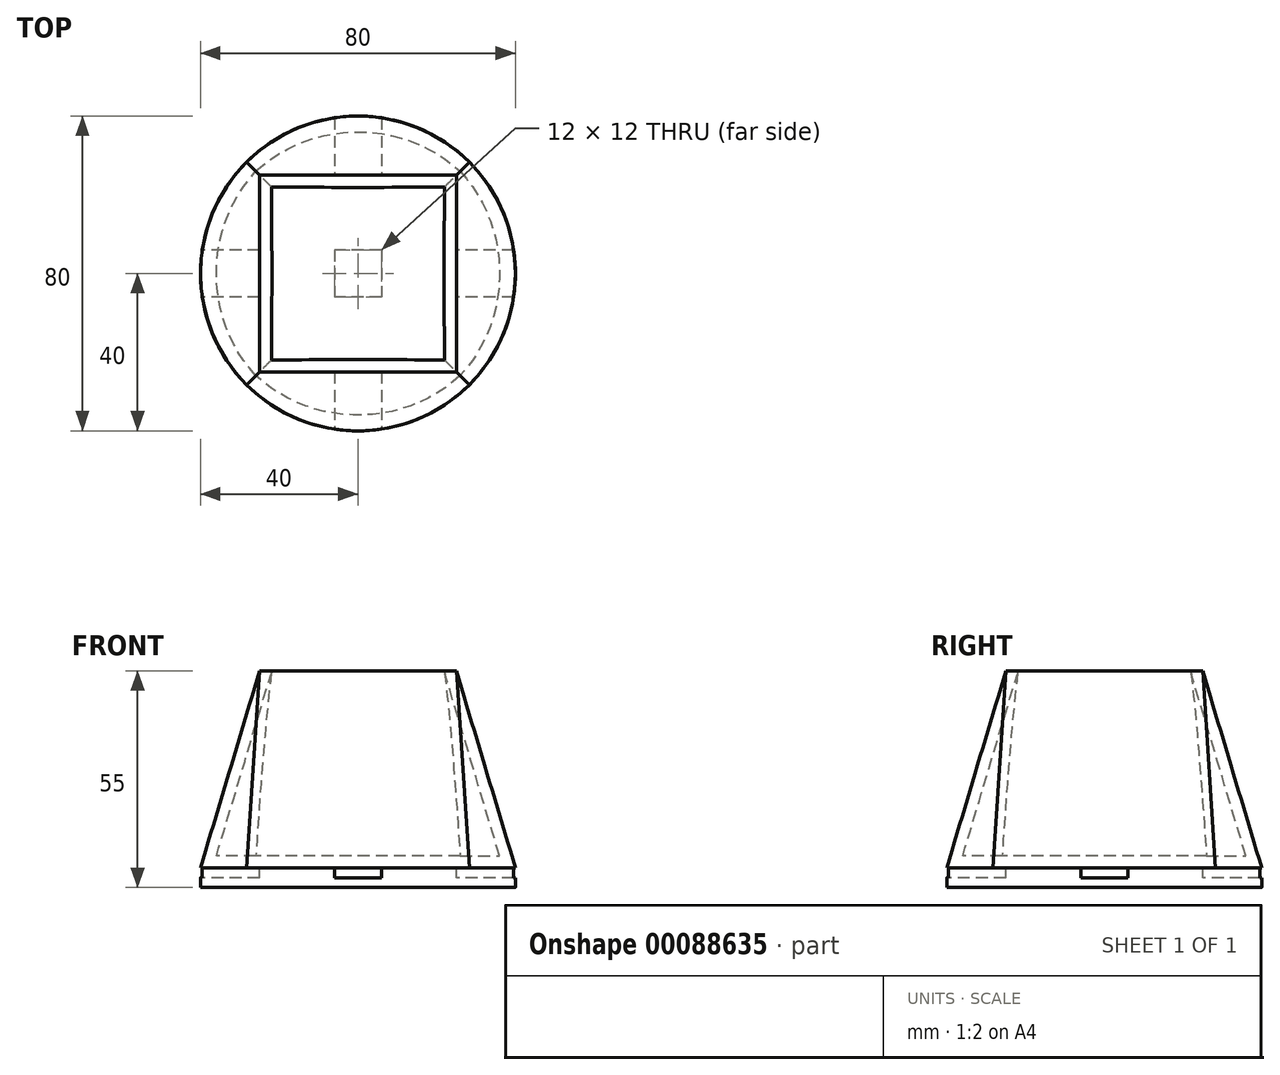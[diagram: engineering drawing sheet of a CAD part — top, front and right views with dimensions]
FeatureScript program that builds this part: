
annotation { "Feature Type Name" : "Feature", "Feature Type Description" : "" }
export const myFeature = defineFeature(function(context is Context, id is Id, definition is map)
    precondition{}
    {
        {
            var Q0;
            Q0=qCreatedBy(makeId("Top.planeOp"),FACE);
            var sketch = newSketch(context, id + "F0", { "sketchPlane" : qUnion([Q0])});
            skCircle(sketch, "E0", {"center": v(0, 0) * mm, "radius": 40 * mm});
            skSolve(sketch);
        }
        {
            var Q0;
            Q0=qCreatedBy(makeId("Top.planeOp"),FACE);
            cPlane(context, id + "F1", {"entities" : qUnion([Q0]), "cplaneType" : CPlaneType.OFFSET, "offset" : 50 * mm, "width" : 152.4 * mm, "height" : 152.4 * mm});
        }
        {
            var Q0;
            Q0=qCreatedBy(id+"F1.planeOp",FACE);
            var sketch = newSketch(context, id + "F2", { "sketchPlane" : qUnion([Q0])});
            skLineSegment(sketch, "E1.bottom", {"start": v(-25, -25) * mm, "end": v(25, -25) * mm});
            skLineSegment(sketch, "E1.top", {"start": v(-25, 25) * mm, "end": v(25, 25) * mm});
            skLineSegment(sketch, "E1.left", {"start": v(-25, -25) * mm, "end": v(-25, 25) * mm});
            skLineSegment(sketch, "E1.right", {"start": v(25, -25) * mm, "end": v(25, 25) * mm});
            skPoint(sketch, "E1.middle", {"position": v(0, 0) * mm});
            skSolve(sketch);
        }
        {
            var Q0;
            Q0=makeQuery(id+"F2.imprint","IMPRINT",FACE,{"disambiguationData":[TD([[makeQuery(id+"F2.imprint","IMPRINT",EDGE,{"derivedFrom":sQuery(id+"F2.wireOp",EDGE,"E1.bottom")}),1.0]])]});
            var Q1;
            Q1=makeQuery(id+"F0.imprint","IMPRINT",FACE,{"disambiguationData":[TD([[makeQuery(id+"F0.imprint","IMPRINT",EDGE,{"derivedFrom":sQuery(id+"F0.wireOp",EDGE,"E0")}),1.0]])]});
            loft(context, id + "F3", {"sheetProfilesArray" : [{ "sheetProfileEntities" : qUnion([Q0]) }, { "sheetProfileEntities" : qUnion([Q1]) }]});
        }
        {
            var Q0;
            Q0=makeQuery(id+"F3.opLoft","CAP_FACE",FACE,{"disambiguationData":[OSD([makeQuery(id+"F2.imprint","IMPRINT",FACE,{"disambiguationData":[TD([[makeQuery(id+"F2.imprint","IMPRINT",EDGE,{"derivedFrom":sQuery(id+"F2.wireOp",EDGE,"E1.bottom")}),1.0]])]})])],"isStart":true});
            shell(context, id + "F4", {"entities" : qUnion([Q0]), "thickness" : 3 * mm});
        }
        {
            var Q0;
            Q0=makeQuery(id+"F3.opLoft","CAP_FACE",FACE,{"disambiguationData":[OSD([makeQuery(id+"F0.imprint","IMPRINT",FACE,{"disambiguationData":[TD([[makeQuery(id+"F0.imprint","IMPRINT",EDGE,{"derivedFrom":sQuery(id+"F0.wireOp",EDGE,"E0")}),1.0]])]})])],"isStart":true});
            var sketch = newSketch(context, id + "F5", { "sketchPlane" : qUnion([Q0])});
            skCircle(sketch, "E2", {"center": v(0, 0) * mm, "radius": 40 * mm});
            skLineSegment(sketch, "E3.bottom", {"start": v(50, -6) * mm, "end": v(-50, -6) * mm});
            skLineSegment(sketch, "E3.top", {"start": v(50, 6) * mm, "end": v(-50, 6) * mm});
            skLineSegment(sketch, "E3.left", {"start": v(50, -6) * mm, "end": v(50, 6) * mm});
            skLineSegment(sketch, "E3.right", {"start": v(-50, -6) * mm, "end": v(-50, 6) * mm});
            skLineSegment(sketch, "E4.bottom", {"start": v(25, -6) * mm, "end": v(-25, -6) * mm});
            skLineSegment(sketch, "E4.top", {"start": v(25, 6) * mm, "end": v(-25, 6) * mm});
            skLineSegment(sketch, "E4.left", {"start": v(25, -6) * mm, "end": v(25, 6) * mm});
            skLineSegment(sketch, "E4.right", {"start": v(-25, -6) * mm, "end": v(-25, 6) * mm});
            skLineSegment(sketch, "E5.bottom", {"start": v(-6, -50) * mm, "end": v(6, -50) * mm});
            skLineSegment(sketch, "E5.top", {"start": v(-6, 50) * mm, "end": v(6, 50) * mm});
            skLineSegment(sketch, "E5.left", {"start": v(-6, -50) * mm, "end": v(-6, 50) * mm});
            skLineSegment(sketch, "E5.right", {"start": v(6, -50) * mm, "end": v(6, 50) * mm});
            skLineSegment(sketch, "E6.bottom", {"start": v(-6, -25) * mm, "end": v(6, -25) * mm});
            skLineSegment(sketch, "E6.top", {"start": v(-6, 25) * mm, "end": v(6, 25) * mm});
            skLineSegment(sketch, "E6.left", {"start": v(-6, -25) * mm, "end": v(-6, 25) * mm});
            skLineSegment(sketch, "E6.right", {"start": v(6, -25) * mm, "end": v(6, 25) * mm});
            skSolve(sketch);
        }
        {
            var Q0;
            {var subQ5=sQuery(id+"F5.wireOp",EDGE,"E2");var subQ6=makeQuery(id+"F5.imprint","IMPRINT",VERTEX,{"disambiguationData":[OD(1.0)],"derivedFrom":subQ5});Q0=makeQuery(id+"F5.imprint","IMPRINT",FACE,{"disambiguationData":[TD([[makeQuery(id+"F5.imprint","IMPRINT",EDGE,{"disambiguationData":[TD([[subQ6,-1.0]])],"derivedFrom":subQ5}),1.0]])]});}
            var Q1;
            {var subQ5=sQuery(id+"F5.wireOp",EDGE,"E6.bottom");Q1=makeQuery(id+"F5.imprint","IMPRINT",FACE,{"disambiguationData":[TD([[makeQuery(id+"F5.imprint","IMPRINT",EDGE,{"derivedFrom":subQ5}),-1.0]])]});}
            var Q2;
            {var subQ3=sQuery(id+"F5.wireOp",EDGE,"E2");var subQ5=makeQuery(id+"F5.imprint","IMPRINT",VERTEX,{"disambiguationData":[OD(0.0)],"derivedFrom":subQ3});Q2=makeQuery(id+"F5.imprint","IMPRINT",FACE,{"disambiguationData":[TD([[makeQuery(id+"F5.imprint","IMPRINT",EDGE,{"disambiguationData":[TD([[subQ5,-1.0]])],"derivedFrom":subQ3}),1.0]])]});}
            var Q3;
            {var subQ5=sQuery(id+"F5.wireOp",EDGE,"E6.bottom");Q3=makeQuery(id+"F5.imprint","IMPRINT",FACE,{"disambiguationData":[TD([[makeQuery(id+"F5.imprint","IMPRINT",EDGE,{"derivedFrom":subQ5}),1.0]])]});}
            var Q4;
            {var subQ0=sQuery(id+"F5.wireOp",EDGE,"E4.right");Q4=makeQuery(id+"F5.imprint","IMPRINT",FACE,{"disambiguationData":[TD([[makeQuery(id+"F5.imprint","IMPRINT",EDGE,{"derivedFrom":subQ0}),-1.0]])]});}
            var Q5;
            {var subQ5=sQuery(id+"F5.wireOp",EDGE,"E4.right");Q5=makeQuery(id+"F5.imprint","IMPRINT",FACE,{"disambiguationData":[TD([[makeQuery(id+"F5.imprint","IMPRINT",EDGE,{"derivedFrom":subQ5}),1.0]])]});}
            var Q6;
            {var subQ5=sQuery(id+"F5.wireOp",EDGE,"E2");var subQ6=makeQuery(id+"F5.imprint","IMPRINT",VERTEX,{"disambiguationData":[OD(3.0)],"derivedFrom":subQ5});Q6=makeQuery(id+"F5.imprint","IMPRINT",FACE,{"disambiguationData":[TD([[makeQuery(id+"F5.imprint","IMPRINT",EDGE,{"disambiguationData":[TD([[subQ6,-1.0]])],"derivedFrom":subQ5}),1.0]])]});}
            var Q7;
            {var subQ5=sQuery(id+"F5.wireOp",EDGE,"E6.top");Q7=makeQuery(id+"F5.imprint","IMPRINT",FACE,{"disambiguationData":[TD([[makeQuery(id+"F5.imprint","IMPRINT",EDGE,{"derivedFrom":subQ5}),-1.0]])]});}
            var Q8;
            {var subQ0=sQuery(id+"F5.wireOp",EDGE,"E6.right");var subQ1=sQuery(id+"F5.wireOp",EDGE,"E4.bottom");var subQ2=makeQuery(id+"F5.imprint","INTERSECT",VERTEX,{"derivedFrom":[subQ1,subQ0]});Q8=makeQuery(id+"F5.imprint","IMPRINT",FACE,{"disambiguationData":[TD([[makeQuery(id+"F5.imprint","IMPRINT",EDGE,{"disambiguationData":[TD([[subQ2,-1.0]])],"derivedFrom":subQ1}),-1.0]])]});}
            var Q9;
            {var subQ0=sQuery(id+"F5.wireOp",EDGE,"E4.left");Q9=makeQuery(id+"F5.imprint","IMPRINT",FACE,{"disambiguationData":[TD([[makeQuery(id+"F5.imprint","IMPRINT",EDGE,{"derivedFrom":subQ0}),1.0]])]});}
            var Q10;
            {var subQ5=sQuery(id+"F5.wireOp",EDGE,"E2");var subQ7=makeQuery(id+"F5.imprint","IMPRINT",VERTEX,{"disambiguationData":[OD(2.0)],"derivedFrom":subQ5});Q10=makeQuery(id+"F5.imprint","IMPRINT",FACE,{"disambiguationData":[TD([[makeQuery(id+"F5.imprint","IMPRINT",EDGE,{"disambiguationData":[TD([[subQ7,-1.0]])],"derivedFrom":subQ5}),1.0]])]});}
            var Q11;
            {var subQ5=sQuery(id+"F5.wireOp",EDGE,"E6.top");Q11=makeQuery(id+"F5.imprint","IMPRINT",FACE,{"disambiguationData":[TD([[makeQuery(id+"F5.imprint","IMPRINT",EDGE,{"derivedFrom":subQ5}),1.0]])]});}
            var Q12;
            {var subQ5=sQuery(id+"F5.wireOp",EDGE,"E4.left");Q12=makeQuery(id+"F5.imprint","IMPRINT",FACE,{"disambiguationData":[TD([[makeQuery(id+"F5.imprint","IMPRINT",EDGE,{"derivedFrom":subQ5}),-1.0]])]});}
            extrude(context, id + "F6", {"entities" : qUnion([Q0, Q1, Q2, Q3, Q4, Q5, Q6, Q7, Q8, Q9, Q10, Q11, Q12]), "depth" : 5 * mm});
        }
        {
            var Q0;
            {var subQ5=sQuery(id+"F5.wireOp",EDGE,"E3.left");Q0=makeQuery(id+"F5.imprint","IMPRINT",FACE,{"disambiguationData":[TD([[makeQuery(id+"F5.imprint","IMPRINT",EDGE,{"derivedFrom":subQ5}),1.0]])]});}
            var Q1;
            {var subQ5=sQuery(id+"F5.wireOp",EDGE,"E4.left");Q1=makeQuery(id+"F5.imprint","IMPRINT",FACE,{"disambiguationData":[TD([[makeQuery(id+"F5.imprint","IMPRINT",EDGE,{"derivedFrom":subQ5}),-1.0]])]});}
            var Q2;
            {var subQ5=sQuery(id+"F5.wireOp",EDGE,"E6.top");Q2=makeQuery(id+"F5.imprint","IMPRINT",FACE,{"disambiguationData":[TD([[makeQuery(id+"F5.imprint","IMPRINT",EDGE,{"derivedFrom":subQ5}),1.0]])]});}
            var Q3;
            {var subQ5=sQuery(id+"F5.wireOp",EDGE,"E5.top");Q3=makeQuery(id+"F5.imprint","IMPRINT",FACE,{"disambiguationData":[TD([[makeQuery(id+"F5.imprint","IMPRINT",EDGE,{"derivedFrom":subQ5}),-1.0]])]});}
            var Q4;
            {var subQ5=sQuery(id+"F5.wireOp",EDGE,"E4.right");Q4=makeQuery(id+"F5.imprint","IMPRINT",FACE,{"disambiguationData":[TD([[makeQuery(id+"F5.imprint","IMPRINT",EDGE,{"derivedFrom":subQ5}),1.0]])]});}
            var Q5;
            {var subQ5=sQuery(id+"F5.wireOp",EDGE,"E3.right");Q5=makeQuery(id+"F5.imprint","IMPRINT",FACE,{"disambiguationData":[TD([[makeQuery(id+"F5.imprint","IMPRINT",EDGE,{"derivedFrom":subQ5}),-1.0]])]});}
            var Q6;
            {var subQ5=sQuery(id+"F5.wireOp",EDGE,"E6.bottom");Q6=makeQuery(id+"F5.imprint","IMPRINT",FACE,{"disambiguationData":[TD([[makeQuery(id+"F5.imprint","IMPRINT",EDGE,{"derivedFrom":subQ5}),-1.0]])]});}
            var Q7;
            {var subQ5=sQuery(id+"F5.wireOp",EDGE,"E5.bottom");Q7=makeQuery(id+"F5.imprint","IMPRINT",FACE,{"disambiguationData":[TD([[makeQuery(id+"F5.imprint","IMPRINT",EDGE,{"derivedFrom":subQ5}),1.0]])]});}
            extrude(context, id + "F7", {"entities" : qUnion([Q0, Q1, Q2, Q3, Q4, Q5, Q6, Q7]), "operationType" : NewBodyOperationType.REMOVE, "depth" : 2.5 * mm});
        }
    });
